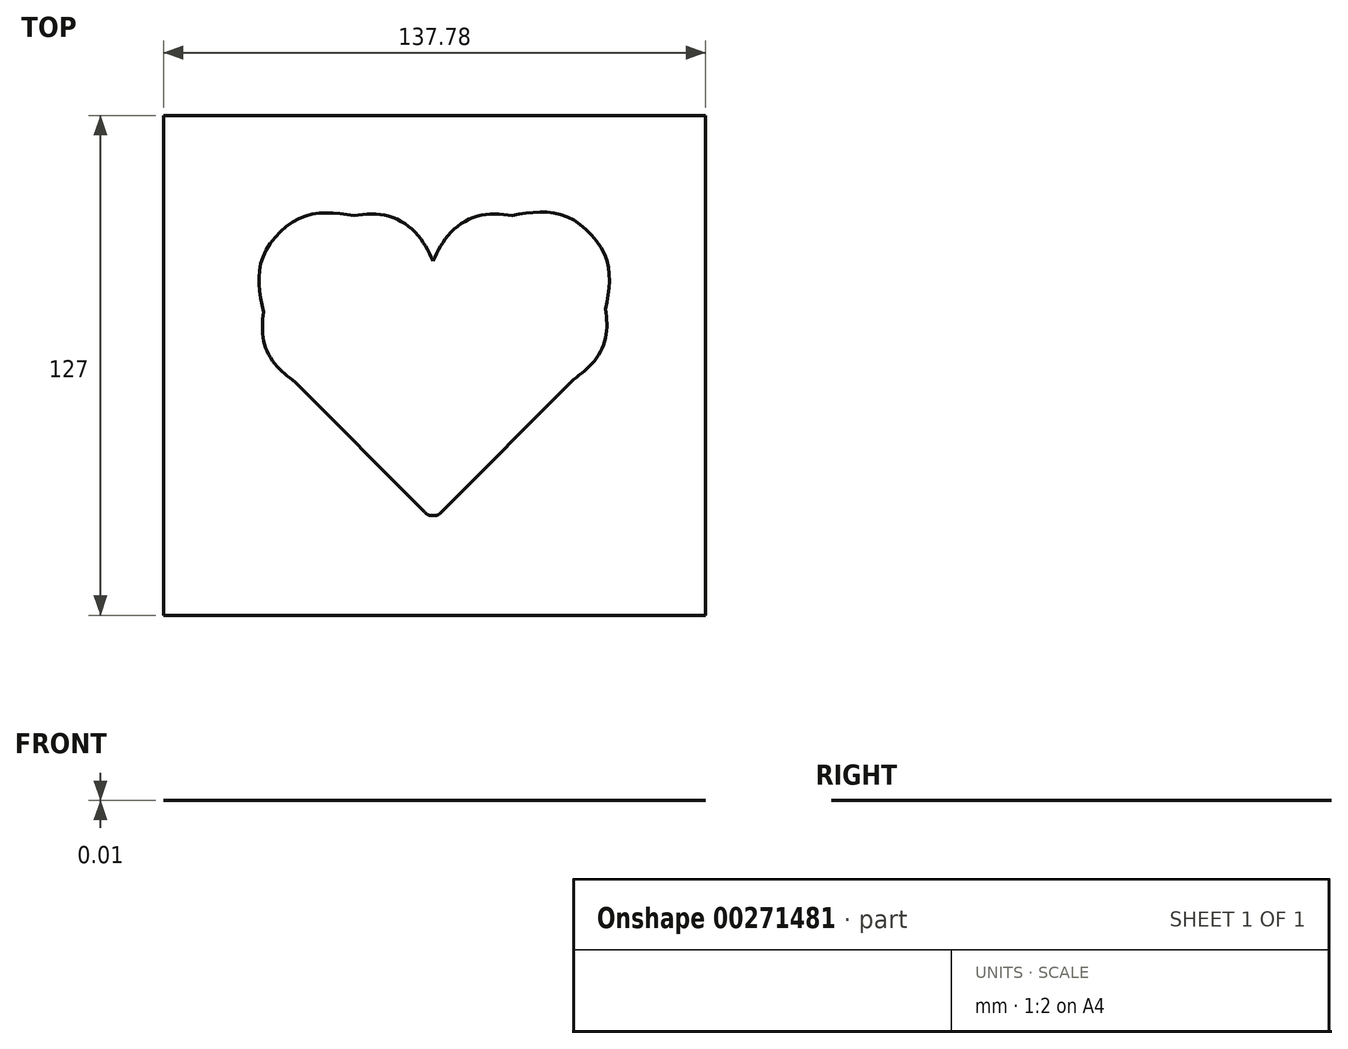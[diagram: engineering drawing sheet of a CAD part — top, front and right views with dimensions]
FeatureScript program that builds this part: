
annotation { "Feature Type Name" : "Feature", "Feature Type Description" : "" }
export const myFeature = defineFeature(function(context is Context, id is Id, definition is map)
    precondition{}
    {
        {
            var Q0;
            Q0=qCreatedBy(makeId("Top.planeOp"),FACE);
            var sketch = newSketch(context, id + "F0", { "sketchPlane" : qUnion([Q0])});
            skFitSpline(sketch, "E0", {"points": [v(43.49, 14.34) * mm, v(43.49, 27.46) * mm, v(32.85, 38.1) * mm, v(19.73, 38.1) * mm]});
            skFitSpline(sketch, "E1", {"points": [v(19.73, 38.1) * mm, v(11.17, 38.01) * mm, v(3.73, 33.4) * mm, v(-0.38, 26.55) * mm]});
            skFitSpline(sketch, "E2", {"points": [v(-0.38, 26.55) * mm, v(-4.5, 33.4) * mm, v(-11.93, 38.01) * mm, v(-20.5, 38.1) * mm]});
            skFitSpline(sketch, "E3", {"points": [v(-20.5, 38.1) * mm, v(-33.61, 37.68) * mm, v(-43.9, 26.72) * mm, v(-43.49, 13.6) * mm]});
            skFitSpline(sketch, "E4", {"points": [v(-43.49, 13.6) * mm, v(-43.49, 6.46) * mm, v(-40.32, 0.07) * mm, v(-35.33, -4.28) * mm]});
            skLineSegment(sketch, "E5", {"start": v(-35.33, -4.28) * mm, "end": v(-2.55, -37.2) * mm});
            skFitSpline(sketch, "E6", {"points": [v(-2.55, -37.2) * mm, v(-1.98, -37.78) * mm, v(-1.2, -38.1) * mm, v(-0.38, -38.1) * mm]});
            skFitSpline(sketch, "E7", {"points": [v(-0.38, -38.1) * mm, v(0.43, -38.1) * mm, v(1.21, -37.78) * mm, v(1.79, -37.2) * mm]});
            skLineSegment(sketch, "E8", {"start": v(1.79, -37.2) * mm, "end": v(35.33, -3.54) * mm});
            skFitSpline(sketch, "E9", {"points": [v(35.33, -3.54) * mm, v(40.32, 0.81) * mm, v(43.49, 7.2) * mm, v(43.49, 14.34) * mm]});
            skLineSegment(sketch, "E10.bottom", {"start": v(68.89, -63.5) * mm, "end": v(-68.89, -63.5) * mm});
            skLineSegment(sketch, "E10.top", {"start": v(68.89, 63.5) * mm, "end": v(-68.89, 63.5) * mm});
            skLineSegment(sketch, "E10.left", {"start": v(68.89, -63.5) * mm, "end": v(68.89, 63.5) * mm});
            skLineSegment(sketch, "E10.right", {"start": v(-68.89, -63.5) * mm, "end": v(-68.89, 63.5) * mm});
            skPoint(sketch, "E10.middle", {"position": v(0, 0) * mm});
            skSolve(sketch);
        }
        {
            var Q0;
            Q0=makeQuery(id+"F0.imprint","IMPRINT",FACE,{"disambiguationData":[TD([[makeQuery(id+"F0.imprint","IMPRINT",EDGE,{"derivedFrom":sQuery(id+"F0.wireOp",EDGE,"E0")}),-1.0]])]});
            var Q1;
            Q1=makeQuery(id+"F0.imprint","IMPRINT",FACE,{"disambiguationData":[TD([[makeQuery(id+"F0.imprint","IMPRINT",EDGE,{"derivedFrom":sQuery(id+"F0.wireOp",EDGE,"E0")}),1.0]])]});
            extrude(context, id + "F1", {"entities" : qUnion([Q0, Q1]), "oppositeDirection" : true, "depth" : 1 / 101.6 * mm});
        }
        {
            var Q0;
            Q0 = qSketchRegion(id + "F0", true);
            var Q1;
            Q1=makeQuery(id+"F1.opExtrude","CAP_FACE",FACE,{"disambiguationData":[OSD([sQuery(id+"F0.wireOp",EDGE,"E10.bottom"),sQuery(id+"F0.wireOp",EDGE,"E10.top"),sQuery(id+"F0.wireOp",EDGE,"E10.left"),sQuery(id+"F0.wireOp",EDGE,"E10.right")])],"isStart":false});
            extrude(context, id + "F2", {"entities" : qUnion([Q0, Q1]), "operationType" : NewBodyOperationType.REMOVE, "oppositeDirection" : true, "depth" : 1 / 203.2 * mm});
        }
    });
